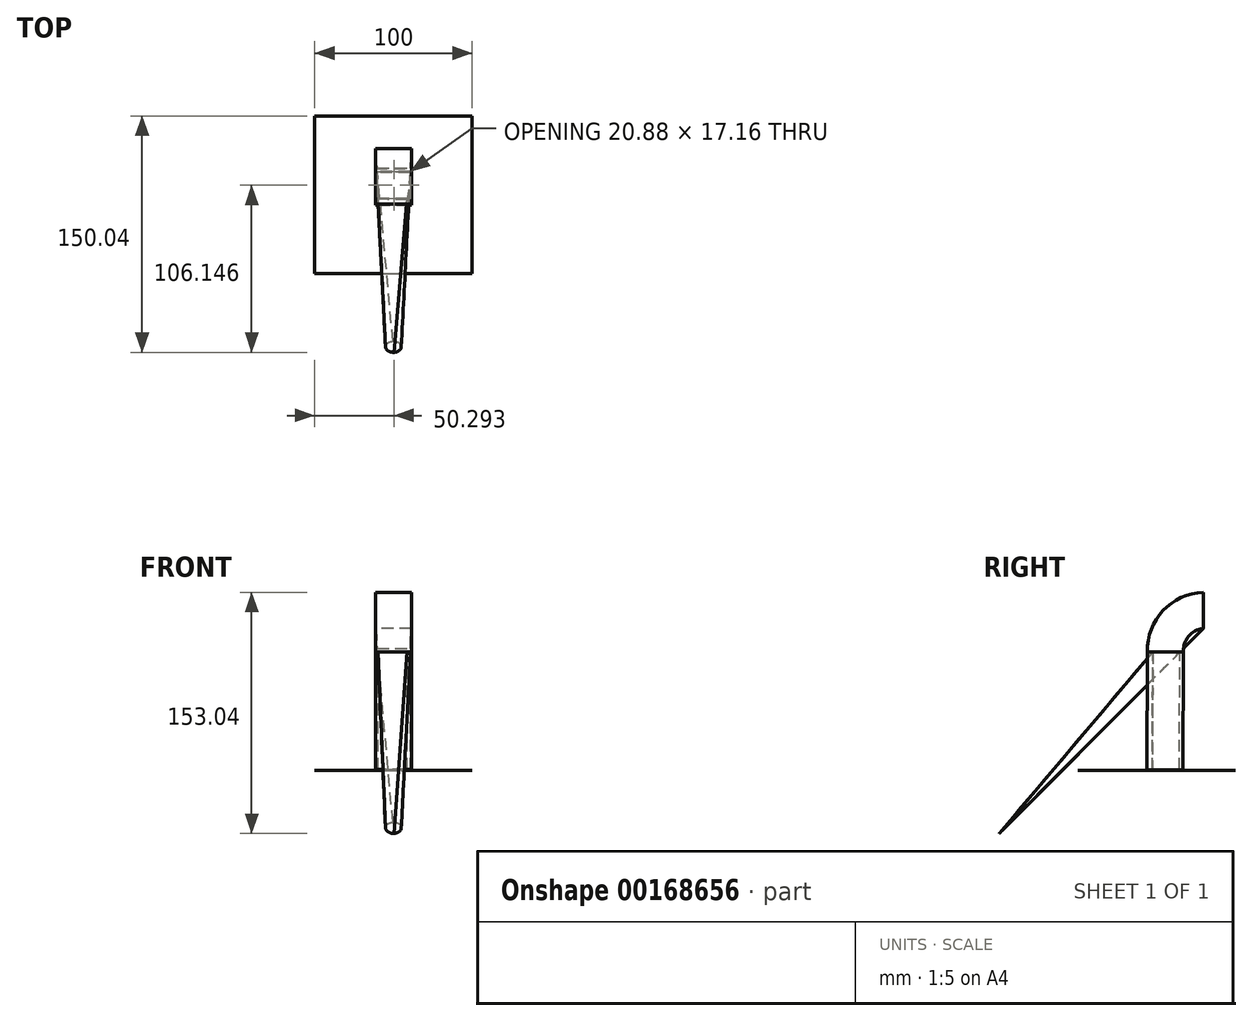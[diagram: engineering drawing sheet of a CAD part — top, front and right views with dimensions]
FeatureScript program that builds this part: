
annotation { "Feature Type Name" : "Feature", "Feature Type Description" : "" }
export const myFeature = defineFeature(function(context is Context, id is Id, definition is map)
    precondition{}
    {
        {
            var Q0;
            Q0=qCreatedBy(makeId("Top.planeOp"),FACE);
            cPlane(context, id + "F0", {"entities" : qUnion([Q0]), "cplaneType" : CPlaneType.OFFSET, "offset" : 96.5 * mm, "width" : 150 * mm, "height" : 150 * mm});
        }
        {
            var Q0;
            Q0=qCreatedBy(id+"F0.planeOp",FACE);
            var sketch = newSketch(context, id + "F1", { "sketchPlane" : qUnion([Q0])});
            skLineSegment(sketch, "E0", {"start": v(-24.4, 36.5) * mm, "end": v(23.96, 36.5) * mm});
            skLineSegment(sketch, "E1", {"start": v(-24.15, 29.5) * mm, "end": v(23.6, 29.5) * mm});
            skSolve(sketch);
        }
        {
            var Q0;
            Q0=sQuery(id+"F1.wireOp",EDGE,"E0");
            cPlane(context, id + "F2", {"entities" : qUnion([Q0]), "cplaneType" : CPlaneType.LINE_ANGLE, "offset" : 25 * mm, "angle" : 315 * degree, "width" : 150 * mm, "height" : 150 * mm});
        }
        {
            var Q0;
            Q0=qCreatedBy(id+"F2.planeOp",FACE);
            var sketch = newSketch(context, id + "F3", { "sketchPlane" : qUnion([Q0])});
            skCircle(sketch, "E2", {"center": v(0, -94.05) * mm, "radius": 5 * mm});
            skSolve(sketch);
        }
        {
            var Q0;
            Q0=sQuery(id+"F1.wireOp",EDGE,"E1");
            cPlane(context, id + "F4", {"entities" : qUnion([Q0]), "cplaneType" : CPlaneType.LINE_ANGLE, "offset" : 25 * mm, "angle" : 0 * degree, "width" : 150 * mm, "height" : 150 * mm});
        }
        {
            var Q0;
            Q0=qCreatedBy(id+"F4.planeOp",FACE);
            var sketch = newSketch(context, id + "F5", { "sketchPlane" : qUnion([Q0])});
            skLineSegment(sketch, "E3.bottom", {"start": v(11.5, 90) * mm, "end": v(-11.5, 90) * mm});
            skLineSegment(sketch, "E3.top", {"start": v(11.5, 113) * mm, "end": v(-11.5, 113) * mm});
            skLineSegment(sketch, "E3.left", {"start": v(11.5, 90) * mm, "end": v(11.5, 113) * mm});
            skLineSegment(sketch, "E3.right", {"start": v(-11.5, 90) * mm, "end": v(-11.5, 113) * mm});
            skPoint(sketch, "E3.middle", {"position": v(0, 101.5) * mm});
            skSolve(sketch);
        }
        {
            var Q0;
            Q0=makeQuery(id+"F3.imprint","IMPRINT",FACE,{"disambiguationData":[TD([[makeQuery(id+"F3.imprint","IMPRINT",EDGE,{"derivedFrom":sQuery(id+"F3.wireOp",EDGE,"E2")}),1.0]])]});
            var Q1;
            Q1=makeQuery(id+"F5.imprint","IMPRINT",FACE,{"disambiguationData":[TD([[makeQuery(id+"F5.imprint","IMPRINT",EDGE,{"derivedFrom":sQuery(id+"F5.wireOp",EDGE,"E3.bottom")}),-1.0]])]});
            loft(context, id + "F6", {"sheetProfilesArray" : [{ "sheetProfileEntities" : qUnion([Q0]) }, { "sheetProfileEntities" : qUnion([Q1]) }]});
        }
        {
            var Q0;
            Q0=qCreatedBy(makeId("Right.planeOp"),FACE);
            var sketch = newSketch(context, id + "F7", { "sketchPlane" : qUnion([Q0])});
            skArc(sketch, "E4", {"start": v(29.03, 101.57) * mm, "mid": v(11.7, 93) * mm, "end": v(5.46, 74.7) * mm});
            skLineSegment(sketch, "E5", {"start": v(5.46, 74.7) * mm, "end": v(5.46, 0) * mm});
            skSolve(sketch);
        }
        {
            var Q0;
            Q0=makeQuery(id+"F5.imprint","IMPRINT",FACE,{"disambiguationData":[TD([[makeQuery(id+"F5.imprint","IMPRINT",EDGE,{"derivedFrom":sQuery(id+"F5.wireOp",EDGE,"E3.bottom")}),-1.0]])]});
            var Q1;
            Q1=sQuery(id+"F7.wireOp",EDGE,"E4");
            sweep(context, id + "F8", {"operationType" : NewBodyOperationType.ADD, "profiles" : qUnion([Q0]), "path" : qUnion([Q1])});
        }
        {
            var Q0;
            Q0=qCreatedBy(makeId("Top.planeOp"),FACE);
            var sketch = newSketch(context, id + "F9", { "sketchPlane" : qUnion([Q0])});
            skLineSegment(sketch, "E6.bottom", {"start": v(-50, 50) * mm, "end": v(50, 50) * mm});
            skLineSegment(sketch, "E6.top", {"start": v(-50, -50) * mm, "end": v(50, -50) * mm});
            skLineSegment(sketch, "E6.left", {"start": v(-50, 50) * mm, "end": v(-50, -50) * mm});
            skLineSegment(sketch, "E6.right", {"start": v(50, 50) * mm, "end": v(50, -50) * mm});
            skPoint(sketch, "E6.middle", {"position": v(0, 0) * mm});
            skSolve(sketch);
        }
        {
            var Q0;
            Q0 = qSketchRegion(id + "F9", true);
            extrude(context, id + "F10", {"entities" : qUnion([Q0]), "operationType" : NewBodyOperationType.ADD, "oppositeDirection" : true, "depth" : 0.01 * mm});
        }
        {
            var Q0;
            Q0=makeQuery(id+"F8.opSweep","CAP_FACE",FACE,{"disambiguationData":[OSD([sQuery(id+"F5.wireOp",EDGE,"E3.bottom"),sQuery(id+"F5.wireOp",EDGE,"E3.top"),sQuery(id+"F5.wireOp",EDGE,"E3.left"),sQuery(id+"F5.wireOp",EDGE,"E3.right"),sQuery(id+"F7.wireOp",VERTEX,"E4.end")])],"isStart":false});
            extrude(context, id + "F11", {"entities" : qUnion([Q0]), "depth" : 74.75 * mm});
        }
    });
